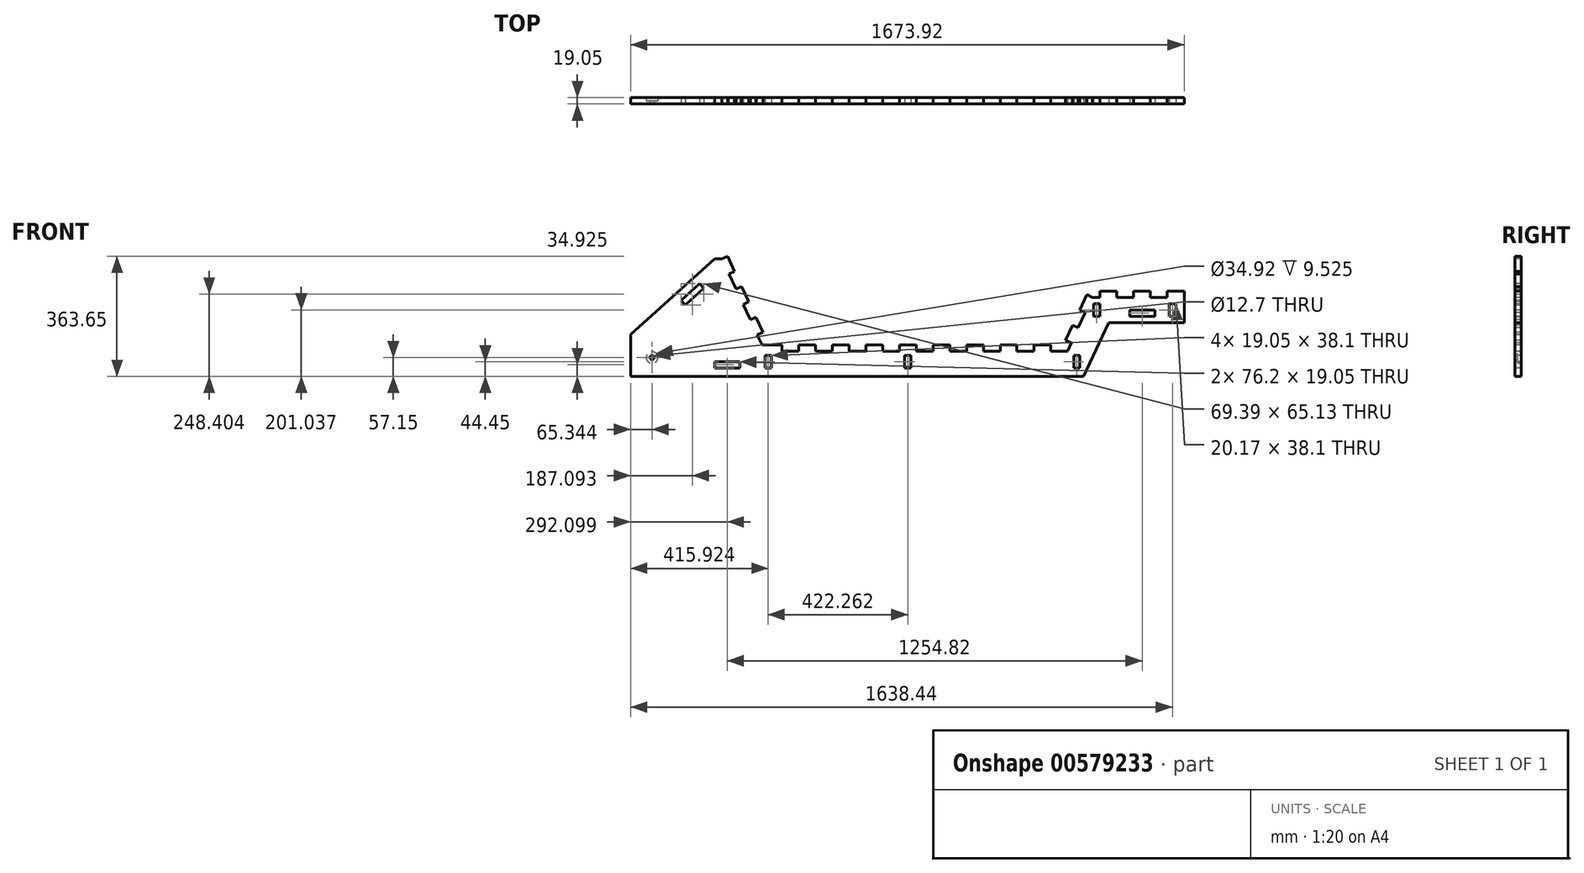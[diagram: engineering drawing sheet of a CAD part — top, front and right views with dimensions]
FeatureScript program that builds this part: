
annotation { "Feature Type Name" : "Feature", "Feature Type Description" : "" }
export const myFeature = defineFeature(function(context is Context, id is Id, definition is map)
    precondition{}
    {
        {
            var Q0;
            Q0=qCreatedBy(makeId("Front.planeOp"),FACE);
            var sketch = newSketch(context, id + "F0", { "sketchPlane" : qUnion([Q0])});
            skLineSegment(sketch, "E0.bottom", {"start": v(-540.23, 76.2) * mm, "end": v(-489.43, 76.2) * mm});
            skLineSegment(sketch, "E0.top", {"start": v(-591.03, 0) * mm, "end": v(342.42, 0) * mm});
            skLineSegment(sketch, "E1", {"start": v(-591.03, 0) * mm, "end": v(-997.43, 0) * mm});
            skLineSegment(sketch, "E2", {"start": v(-721.32, 355.6) * mm, "end": v(-743.43, 355.6) * mm});
            skLineSegment(sketch, "E3", {"start": v(-699.85, 309.56) * mm, "end": v(-678.38, 263.52) * mm});
            skLineSegment(sketch, "E4.MirrorCS", {"start": v(399.26, 239.14) * mm, "end": v(421.37, 239.14) * mm});
            skLineSegment(sketch, "E5.MirrorCS", {"start": v(377.79, 193.1) * mm, "end": v(356.32, 147.06) * mm});
            skLineSegment(sketch, "E6", {"start": v(676.5, 239.14) * mm, "end": v(676.5, 162.94) * mm});
            skLineSegment(sketch, "E7", {"start": v(676.5, 162.94) * mm, "end": v(502.2, 162.94) * mm});
            skLineSegment(sketch, "E8", {"start": v(342.42, 0) * mm, "end": v(371.91, 0) * mm});
            skLineSegment(sketch, "E9", {"start": v(392.43, 44) * mm, "end": v(371.91, 0) * mm});
            skLineSegment(sketch, "E10.top", {"start": v(-286.23, 95.25) * mm, "end": v(-235.43, 95.25) * mm});
            skLineSegment(sketch, "E10.left", {"start": v(-286.23, 76.2) * mm, "end": v(-286.23, 95.25) * mm});
            skLineSegment(sketch, "E10.right", {"start": v(-235.43, 76.2) * mm, "end": v(-235.43, 95.25) * mm});
            skLineSegment(sketch, "E11.bottom", {"start": v(-656.9, 217.48) * mm, "end": v(-635.44, 171.44) * mm});
            skLineSegment(sketch, "E11.left", {"start": v(-656.9, 217.48) * mm, "end": v(-639.64, 225.53) * mm});
            skLineSegment(sketch, "E11.right", {"start": v(-635.44, 171.44) * mm, "end": v(-618.18, 179.49) * mm});
            skLineSegment(sketch, "E12.top", {"start": v(-661.11, 271.57) * mm, "end": v(-639.64, 225.53) * mm});
            skLineSegment(sketch, "E12.left", {"start": v(-678.38, 263.52) * mm, "end": v(-661.11, 271.57) * mm});
            skLineSegment(sketch, "E13.left", {"start": v(-699.85, 309.56) * mm, "end": v(-682.58, 317.61) * mm});
            skLineSegment(sketch, "E14.top", {"start": v(-704.05, 363.65) * mm, "end": v(-682.58, 317.61) * mm});
            skLineSegment(sketch, "E14.left", {"start": v(-721.32, 355.6) * mm, "end": v(-704.05, 363.65) * mm});
            skLineSegment(sketch, "E15.top", {"start": v(-618.18, 179.49) * mm, "end": v(-596.7, 133.45) * mm});
            skLineSegment(sketch, "E15.right", {"start": v(-613.97, 125.4) * mm, "end": v(-596.7, 133.45) * mm});
            skLineSegment(sketch, "E16.bottom", {"start": v(-613.97, 125.4) * mm, "end": v(-599.91, 95.25) * mm});
            skLineSegment(sketch, "E17.top", {"start": v(-591.03, 95.25) * mm, "end": v(-540.23, 95.25) * mm});
            skLineSegment(sketch, "E17.right", {"start": v(-540.23, 76.2) * mm, "end": v(-540.23, 95.25) * mm});
            skLineSegment(sketch, "E18.right", {"start": v(-489.43, 76.2) * mm, "end": v(-489.43, 95.25) * mm});
            skLineSegment(sketch, "E19.top", {"start": v(-387.83, 95.25) * mm, "end": v(-337.03, 95.25) * mm});
            skLineSegment(sketch, "E19.left", {"start": v(-387.83, 76.2) * mm, "end": v(-387.83, 95.25) * mm});
            skLineSegment(sketch, "E19.right", {"start": v(-337.03, 76.2) * mm, "end": v(-337.03, 95.25) * mm});
            skLineSegment(sketch, "E20.top", {"start": v(-489.43, 95.25) * mm, "end": v(-438.63, 95.25) * mm});
            skLineSegment(sketch, "E20.right", {"start": v(-438.63, 76.2) * mm, "end": v(-438.63, 95.25) * mm});
            skLineSegment(sketch, "E21.bottom", {"start": v(-337.03, 76.2) * mm, "end": v(-286.23, 76.2) * mm});
            skLineSegment(sketch, "E22.bottom", {"start": v(-438.63, 76.2) * mm, "end": v(-387.83, 76.2) * mm});
            skLineSegment(sketch, "E23.bottom", {"start": v(-32.23, 76.2) * mm, "end": v(18.57, 76.2) * mm});
            skLineSegment(sketch, "E23.left", {"start": v(-32.23, 76.2) * mm, "end": v(-32.23, 95.25) * mm});
            skLineSegment(sketch, "E23.right", {"start": v(18.57, 76.2) * mm, "end": v(18.57, 95.25) * mm});
            skLineSegment(sketch, "E24.top", {"start": v(-184.63, 95.25) * mm, "end": v(-133.83, 95.25) * mm});
            skLineSegment(sketch, "E24.left", {"start": v(-184.63, 76.2) * mm, "end": v(-184.63, 95.25) * mm});
            skLineSegment(sketch, "E24.right", {"start": v(-133.83, 76.2) * mm, "end": v(-133.83, 95.25) * mm});
            skLineSegment(sketch, "E25.top", {"start": v(18.57, 95.25) * mm, "end": v(69.37, 95.25) * mm});
            skLineSegment(sketch, "E25.right", {"start": v(69.37, 76.2) * mm, "end": v(69.37, 95.25) * mm});
            skLineSegment(sketch, "E26.bottom", {"start": v(-133.83, 76.2) * mm, "end": v(-83.03, 76.2) * mm});
            skLineSegment(sketch, "E26.right", {"start": v(-83.03, 76.2) * mm, "end": v(-83.03, 95.25) * mm});
            skLineSegment(sketch, "E27.top", {"start": v(-83.03, 95.25) * mm, "end": v(-32.23, 95.25) * mm});
            skLineSegment(sketch, "E28.bottom", {"start": v(-235.43, 76.2) * mm, "end": v(-184.63, 76.2) * mm});
            skLineSegment(sketch, "E29.bottom", {"start": v(170.97, 76.2) * mm, "end": v(221.77, 76.2) * mm});
            skLineSegment(sketch, "E29.left", {"start": v(170.97, 76.2) * mm, "end": v(170.97, 95.25) * mm});
            skLineSegment(sketch, "E29.right", {"start": v(221.77, 76.2) * mm, "end": v(221.77, 95.25) * mm});
            skLineSegment(sketch, "E30.bottom", {"start": v(69.37, 76.2) * mm, "end": v(120.17, 76.2) * mm});
            skLineSegment(sketch, "E30.right", {"start": v(120.17, 76.2) * mm, "end": v(120.17, 95.25) * mm});
            skLineSegment(sketch, "E31.top", {"start": v(221.77, 95.25) * mm, "end": v(272.57, 95.25) * mm});
            skLineSegment(sketch, "E31.right", {"start": v(272.57, 76.2) * mm, "end": v(272.57, 95.25) * mm});
            skLineSegment(sketch, "E32.top", {"start": v(120.17, 95.25) * mm, "end": v(170.97, 95.25) * mm});
            skLineSegment(sketch, "E33.bottom", {"start": v(272.57, 76.2) * mm, "end": v(323.37, 76.2) * mm});
            skLineSegment(sketch, "E34", {"start": v(-591.03, 95.25) * mm, "end": v(-599.91, 95.25) * mm});
            skLineSegment(sketch, "E35.top", {"start": v(624.57, 258.19) * mm, "end": v(676.5, 258.19) * mm});
            skLineSegment(sketch, "E35.left", {"start": v(624.57, 239.14) * mm, "end": v(624.57, 258.19) * mm});
            skLineSegment(sketch, "E35.right", {"start": v(676.5, 239.14) * mm, "end": v(676.5, 258.19) * mm});
            skLineSegment(sketch, "E36.top", {"start": v(522.97, 258.19) * mm, "end": v(573.77, 258.19) * mm});
            skLineSegment(sketch, "E36.left", {"start": v(522.97, 239.14) * mm, "end": v(522.97, 258.19) * mm});
            skLineSegment(sketch, "E36.right", {"start": v(573.77, 239.14) * mm, "end": v(573.77, 258.19) * mm});
            skLineSegment(sketch, "E37.bottom", {"start": v(573.77, 239.14) * mm, "end": v(624.57, 239.14) * mm});
            skLineSegment(sketch, "E38.bottom", {"start": v(472.17, 239.14) * mm, "end": v(522.97, 239.14) * mm});
            skLineSegment(sketch, "E38.left", {"start": v(472.17, 239.14) * mm, "end": v(472.17, 258.19) * mm});
            skLineSegment(sketch, "E39.top", {"start": v(421.37, 258.19) * mm, "end": v(472.17, 258.19) * mm});
            skLineSegment(sketch, "E39.left", {"start": v(421.37, 239.14) * mm, "end": v(421.37, 258.19) * mm});
            skLineSegment(sketch, "E40.bottom", {"start": v(382, 247.19) * mm, "end": v(360.52, 201.15) * mm});
            skLineSegment(sketch, "E40.left", {"start": v(382, 247.19) * mm, "end": v(399.26, 239.14) * mm});
            skLineSegment(sketch, "E40.right", {"start": v(360.52, 201.15) * mm, "end": v(377.79, 193.1) * mm});
            skLineSegment(sketch, "E41.bottom", {"start": v(339.05, 155.1) * mm, "end": v(317.58, 109.06) * mm});
            skLineSegment(sketch, "E41.left", {"start": v(339.05, 155.1) * mm, "end": v(356.32, 147.06) * mm});
            skLineSegment(sketch, "E42.bottom", {"start": v(-591.03, 25.4) * mm, "end": v(-571.98, 25.4) * mm});
            skLineSegment(sketch, "E42.top", {"start": v(-591.03, 63.5) * mm, "end": v(-571.98, 63.5) * mm});
            skLineSegment(sketch, "E42.left", {"start": v(-591.03, 25.4) * mm, "end": v(-591.03, 63.5) * mm});
            skLineSegment(sketch, "E42.right", {"start": v(-571.98, 25.4) * mm, "end": v(-571.98, 63.5) * mm});
            skLineSegment(sketch, "E43.bottom", {"start": v(-168.77, 25.4) * mm, "end": v(-149.72, 25.4) * mm});
            skLineSegment(sketch, "E43.top", {"start": v(-168.77, 63.5) * mm, "end": v(-149.72, 63.5) * mm});
            skLineSegment(sketch, "E43.left", {"start": v(-168.77, 25.4) * mm, "end": v(-168.77, 63.5) * mm});
            skLineSegment(sketch, "E43.right", {"start": v(-149.72, 25.4) * mm, "end": v(-149.72, 63.5) * mm});
            skLineSegment(sketch, "E44.bottom", {"start": v(342.42, 25.4) * mm, "end": v(361.47, 25.4) * mm});
            skLineSegment(sketch, "E44.top", {"start": v(342.42, 63.5) * mm, "end": v(361.47, 63.5) * mm});
            skLineSegment(sketch, "E44.left", {"start": v(342.42, 25.4) * mm, "end": v(342.42, 63.5) * mm});
            skLineSegment(sketch, "E44.right", {"start": v(361.47, 25.4) * mm, "end": v(361.47, 63.5) * mm});
            skLineSegment(sketch, "E45.bottom", {"start": v(630.92, 181.99) * mm, "end": v(651.1, 181.99) * mm});
            skLineSegment(sketch, "E45.top", {"start": v(630.92, 220.09) * mm, "end": v(651.1, 220.09) * mm});
            skLineSegment(sketch, "E45.left", {"start": v(630.92, 181.99) * mm, "end": v(630.92, 220.09) * mm});
            skLineSegment(sketch, "E45.right", {"start": v(651.1, 181.99) * mm, "end": v(651.1, 220.09) * mm});
            skLineSegment(sketch, "E46.bottom", {"start": v(402.32, 181.99) * mm, "end": v(421.37, 181.99) * mm});
            skLineSegment(sketch, "E46.top", {"start": v(402.32, 220.09) * mm, "end": v(421.37, 220.09) * mm});
            skLineSegment(sketch, "E46.left", {"start": v(402.32, 181.99) * mm, "end": v(402.32, 220.09) * mm});
            skLineSegment(sketch, "E46.right", {"start": v(421.37, 181.99) * mm, "end": v(421.37, 220.09) * mm});
            skCircle(sketch, "E47", {"center": v(-932.09, 57.15) * mm, "radius": 6.35 * mm});
            skCircle(sketch, "E48", {"center": v(-932.09, 57.15) * mm, "radius": 17.46 * mm});
            skLineSegment(sketch, "E49", {"start": v(317.58, 109.06) * mm, "end": v(334.84, 101) * mm});
            skLineSegment(sketch, "E50", {"start": v(334.84, 101) * mm, "end": v(323.37, 76.2) * mm});
            skLineSegment(sketch, "E51", {"start": v(502.2, 162.94) * mm, "end": v(447.9, 162.94) * mm});
            skLineSegment(sketch, "E52", {"start": v(392.43, 44) * mm, "end": v(447.9, 162.94) * mm});
            skLineSegment(sketch, "E53.bottom", {"start": v(-667.23, 44.45) * mm, "end": v(-743.43, 44.45) * mm});
            skLineSegment(sketch, "E53.top", {"start": v(-667.23, 25.4) * mm, "end": v(-743.43, 25.4) * mm});
            skLineSegment(sketch, "E53.left", {"start": v(-667.23, 44.45) * mm, "end": v(-667.23, 25.4) * mm});
            skLineSegment(sketch, "E53.right", {"start": v(-743.43, 44.45) * mm, "end": v(-743.43, 25.4) * mm});
            skLineSegment(sketch, "E54.bottom", {"start": v(511.4, 201.04) * mm, "end": v(587.6, 201.04) * mm});
            skLineSegment(sketch, "E54.top", {"start": v(511.4, 181.99) * mm, "end": v(587.6, 181.99) * mm});
            skLineSegment(sketch, "E54.left", {"start": v(511.4, 201.04) * mm, "end": v(511.4, 181.99) * mm});
            skLineSegment(sketch, "E54.right", {"start": v(587.6, 201.04) * mm, "end": v(587.6, 181.99) * mm});
            skLineSegment(sketch, "E55", {"start": v(-997.43, 0) * mm, "end": v(-997.43, 127) * mm});
            skLineSegment(sketch, "E56", {"start": v(-743.43, 355.6) * mm, "end": v(-997.43, 127) * mm});
            skLineSegment(sketch, "E57.bottom", {"start": v(-845.03, 230) * mm, "end": v(-788.39, 280.97) * mm});
            skLineSegment(sketch, "E57.top", {"start": v(-832.29, 215.84) * mm, "end": v(-775.64, 266.8) * mm});
            skLineSegment(sketch, "E57.right", {"start": v(-788.39, 280.97) * mm, "end": v(-775.64, 266.8) * mm});
            skLineSegment(sketch, "E58", {"start": v(-845.03, 230) * mm, "end": v(-832.29, 215.84) * mm});
            skSolve(sketch);
        }
        {
            var Q0;
            Q0=makeQuery(id+"F0.imprint","IMPRINT",FACE,{"disambiguationData":[TD([[makeQuery(id+"F0.imprint","IMPRINT",EDGE,{"derivedFrom":sQuery(id+"F0.wireOp",EDGE,"E0.top")}),1.0]])]});
            extrude(context, id + "F1", {"entities" : qUnion([Q0]), "oppositeDirection" : true, "depth" : 19.05 * mm, "offsetDistance" : 25.4 * mm});
        }
        {
            var Q0;
            Q0=makeQuery(id+"F0.imprint","IMPRINT",FACE,{"disambiguationData":[TD([[makeQuery(id+"F0.imprint","IMPRINT",EDGE,{"derivedFrom":sQuery(id+"F0.wireOp",EDGE,"E47")}),-1.0]])]});
            extrude(context, id + "F2", {"entities" : qUnion([Q0]), "operationType" : NewBodyOperationType.ADD, "oppositeDirection" : true, "depth" : 9.52 * mm, "offsetDistance" : 25.4 * mm});
        }
    });
